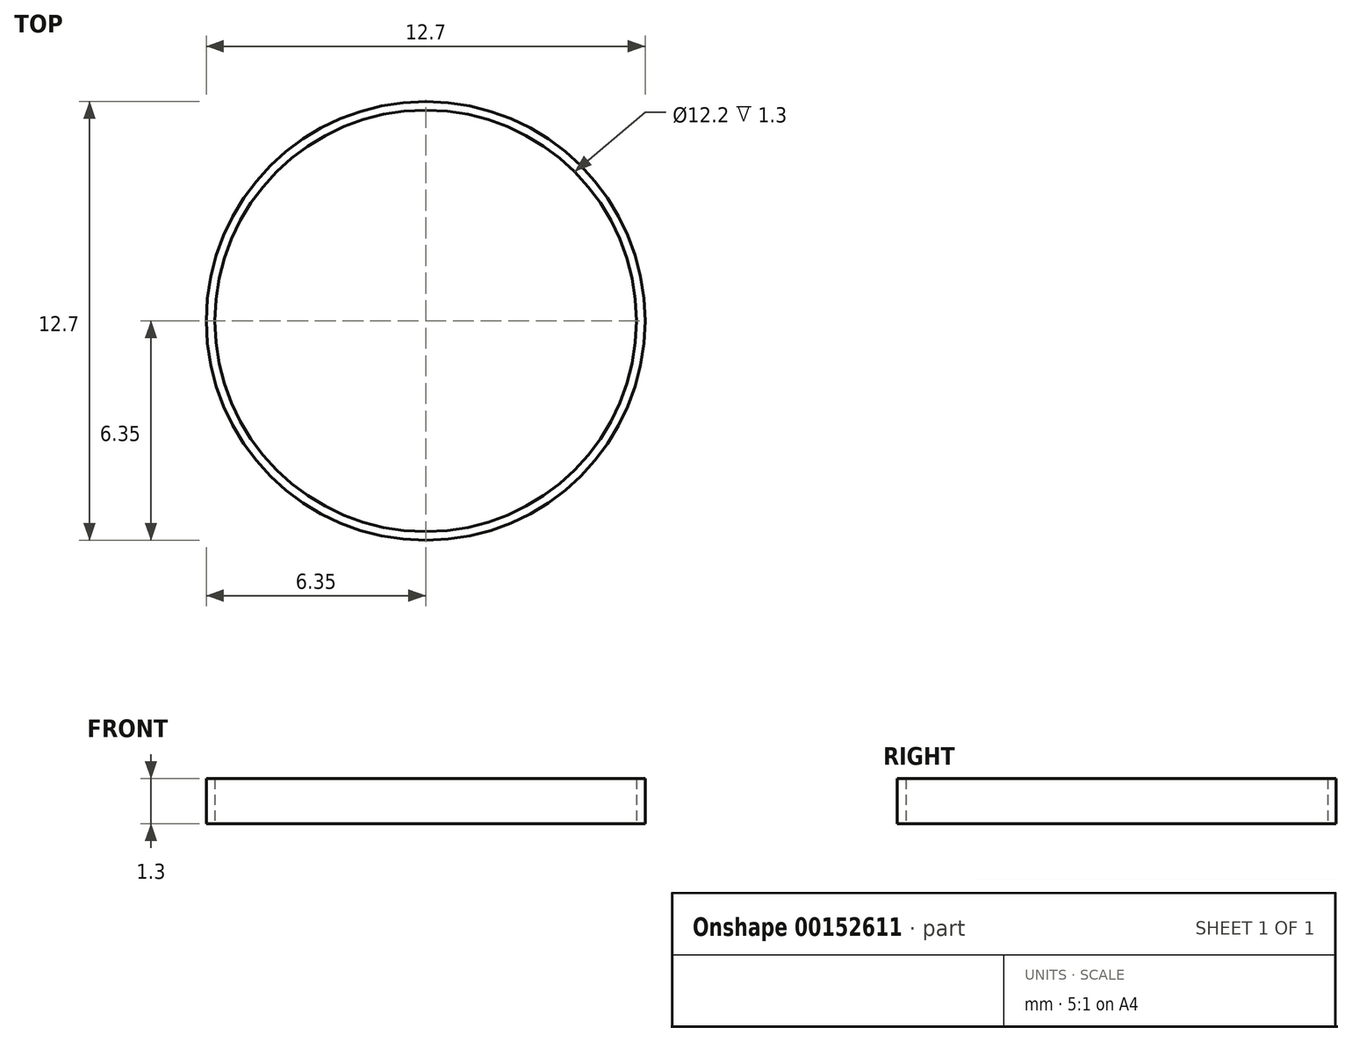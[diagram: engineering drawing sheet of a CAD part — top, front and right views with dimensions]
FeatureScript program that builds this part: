
annotation { "Feature Type Name" : "Feature", "Feature Type Description" : "" }
export const myFeature = defineFeature(function(context is Context, id is Id, definition is map)
    precondition{}
    {
        {
            var Q0;
            Q0=qCreatedBy(makeId("Top.planeOp"),FACE);
            var sketch = newSketch(context, id + "F0", { "sketchPlane" : qUnion([Q0])});
            skCircle(sketch, "E0", {"center": v(0, 0) * mm, "radius": 6.35 * mm});
            skCircle(sketch, "E1", {"center": v(0, 0) * mm, "radius": 6.1 * mm});
            skSolve(sketch);
        }
        {
            var Q0;
            Q0=makeQuery(id+"F0.imprint","IMPRINT",FACE,{"disambiguationData":[TD([[makeQuery(id+"F0.imprint","IMPRINT",EDGE,{"derivedFrom":sQuery(id+"F0.wireOp",EDGE,"E0")}),1.0]])]});
            extrude(context, id + "F1", {"entities" : qUnion([Q0]), "depth" : 1.3 * mm});
        }
    });
